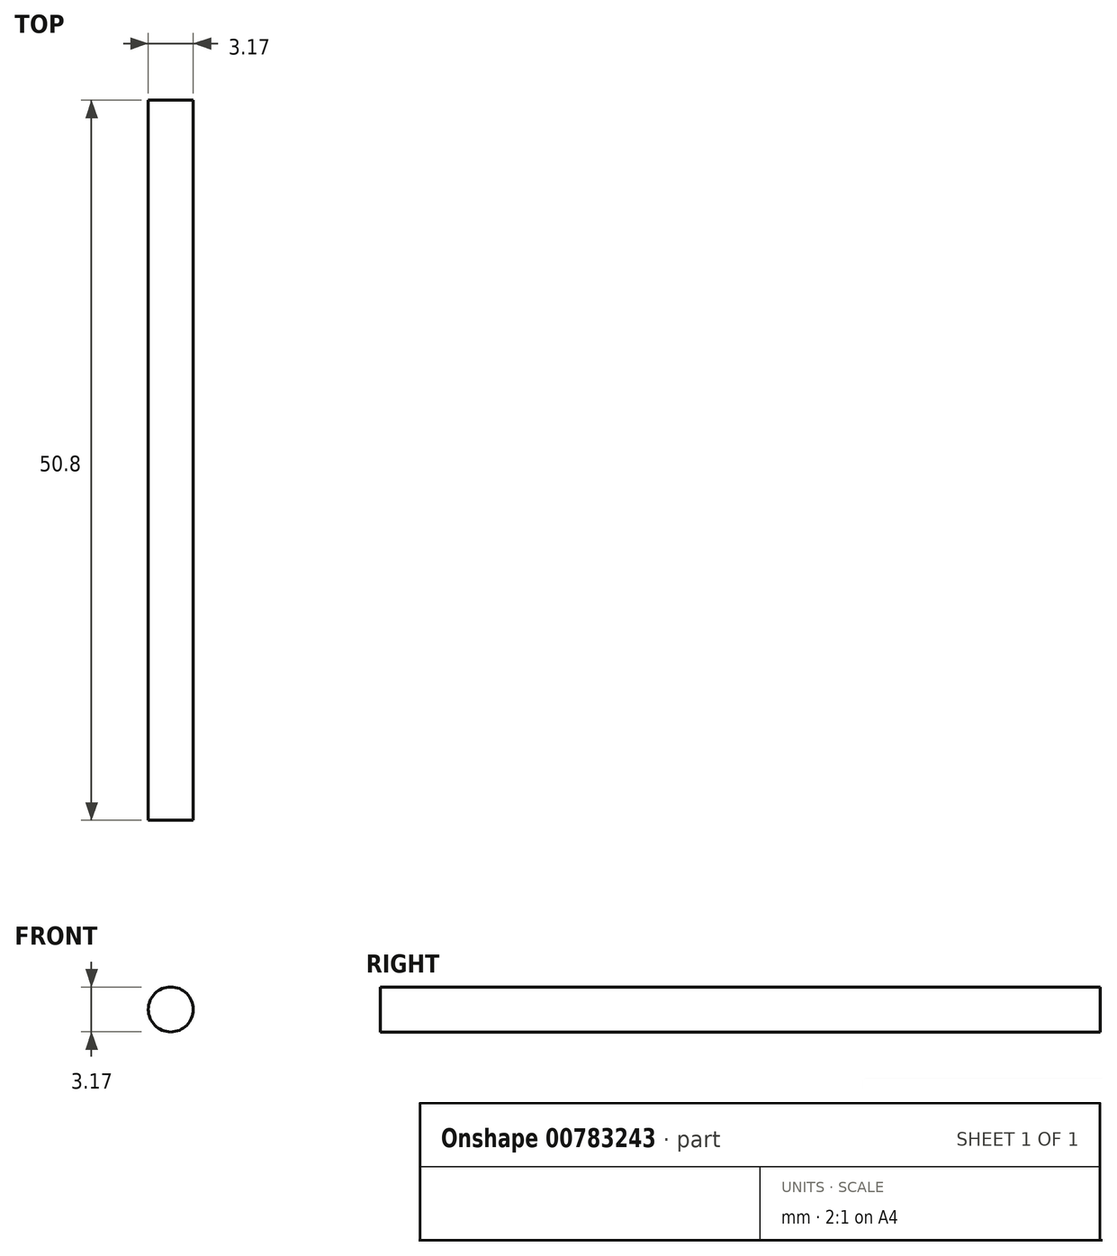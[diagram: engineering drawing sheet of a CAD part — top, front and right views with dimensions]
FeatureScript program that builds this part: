
annotation { "Feature Type Name" : "Feature", "Feature Type Description" : "" }
export const myFeature = defineFeature(function(context is Context, id is Id, definition is map)
    precondition{}
    {
        {
            var Q0;
            Q0=qCreatedBy(makeId("Front.planeOp"),FACE);
            var sketch = newSketch(context, id + "F0", { "sketchPlane" : qUnion([Q0])});
            skCircle(sketch, "E0", {"center": v(-22.9, 28.18) * mm, "radius": 1.59 * mm});
            skSolve(sketch);
        }
        {
            var Q0;
            Q0=makeQuery(id+"F0.imprint","IMPRINT",FACE,{"disambiguationData":[TD([[makeQuery(id+"F0.imprint","IMPRINT",EDGE,{"derivedFrom":sQuery(id+"F0.wireOp",EDGE,"E0")}),1.0]])]});
            extrude(context, id + "F1", {"entities" : qUnion([Q0]), "depth" : 50.8 * mm, "offsetDistance" : 25.4 * mm});
        }
    });
